# Revit family: QF_TRUE_T-72FG-HC~FGD01
name_source: partatom
category: Specialty Equipment
revit_build: Autodesk Revit 2015 (Build: 20140606_1530(x64)
units: mm (PartAtom-declared; Revit-internal decimal feet)

## types (1)
- QF_TRUE_T-72FG-HC~FGD01
    Apparent Power = 0 VA
    Body Height = 78 3/8"
    Conn Conduit = Yes
    Conn Plug = NEMA-5-20P
    Cycle = 60 Hz
    Depth = 29 7/8"
    Description = REACH-IN GLASS SWING DOOR - 10ºF FREEZER WITH HYDROCARBON REFRIGERANT~FRAMED GLASS DOOR VERSION 01
    Elec Conn Connection Height = 0"
    Elec Conn RI Height = 0"
    FL Amps = 13 A
    Foodservice Equipment Identifier = Yes
    HP = 3/4
    Height = 83 3/8"
    Identify Quantity as Lot = Yes
    Length = 78 1/8"
    Manufacturer = TRUE
    Max Overcurrent Protection = 0 A
    Min Ckt Ampacity = 0 A
    Model = T-72FG-HC-FGD01
    Number of Poles = 1
    Phase = 1
    URL = www.truemfg.com
    URL Cutsheet = www.truemfg.com
    Volts = 115 V
    Watts = 1495 W
    Weight in Pounds = 760

## geometry (parser evidence)
native form markers: Blend x2, Sweep x19
no freeform markers — native parametric forms only
